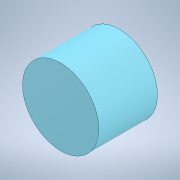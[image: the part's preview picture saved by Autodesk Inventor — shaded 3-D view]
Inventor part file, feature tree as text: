
AUTODESK INVENTOR PART (.ipt)
format: ipt  version: 2022 (Build 260153000, 153)  size: 100,864 bytes
history: native  units: in
note: dims shown in document units (in); Inventor stores cm internally (conversion verified against a paired STEP export)
features: extrude x1, sketch x1
ambient origin geometry x8: Origin, YZ Plane, XZ Plane, XY Plane, X Axis, Y Axis, Z Axis, Center Point
bodies: Solid1 (feature_tree)
feature tree (2):
  extrude  "Extrusion1"  Depth=0.1969in
  sketch  "Sketch2"  dims[d0=0.1969in d1=0.0in d2=0.2559in]
